# Revit family: Lighting-Surface-Amerlux-Linea 3.5
name_source: partatom
category: Lighting Fixtures
revit_build: Autodesk Revit LT 2014 (Build: 20130308_1515(x64)
units: mm (PartAtom-declared; Revit-internal decimal feet)

## types (3) — shared parameters
Apparent Load = 0 VA
Color Filter = 16777215
Default Elevation = 4' - 0"
Description = Surface Linea 3.5"
Dimming Lamp Color Temperature Shift = <None>
Emit Shape Visible in Rendering = No
Emit from Circle Diameter = 0' - 1 1/4"
Fixture Finish = White
IES File Link = http://www.amerlux.com
Lamp = LED
Length = 4' - 0"
Manufacturer = Amerlux
Number of Poles = 1
Photometric Web File = generic
Power Factor = 1
Tilt Angle = -90.00°
URL = http://www.amerlux.com
Voltage = 0 V

## per-type parameters (varying)
| type | Height | Model | Width |
| Direct | 0' - 3 5/8" | LS35D | 0' - 3 7/16" |
| Indirect | 0' - 3 5/8" | LS35I | 0' - 2 7/8" |
| Direct/Indirect | 0' - 5 7/8" | LS35DI | 0' - 2 7/8" |

## geometry (parser evidence)
native form markers: Blend x4, Sweep x1
no freeform markers — native parametric forms only
